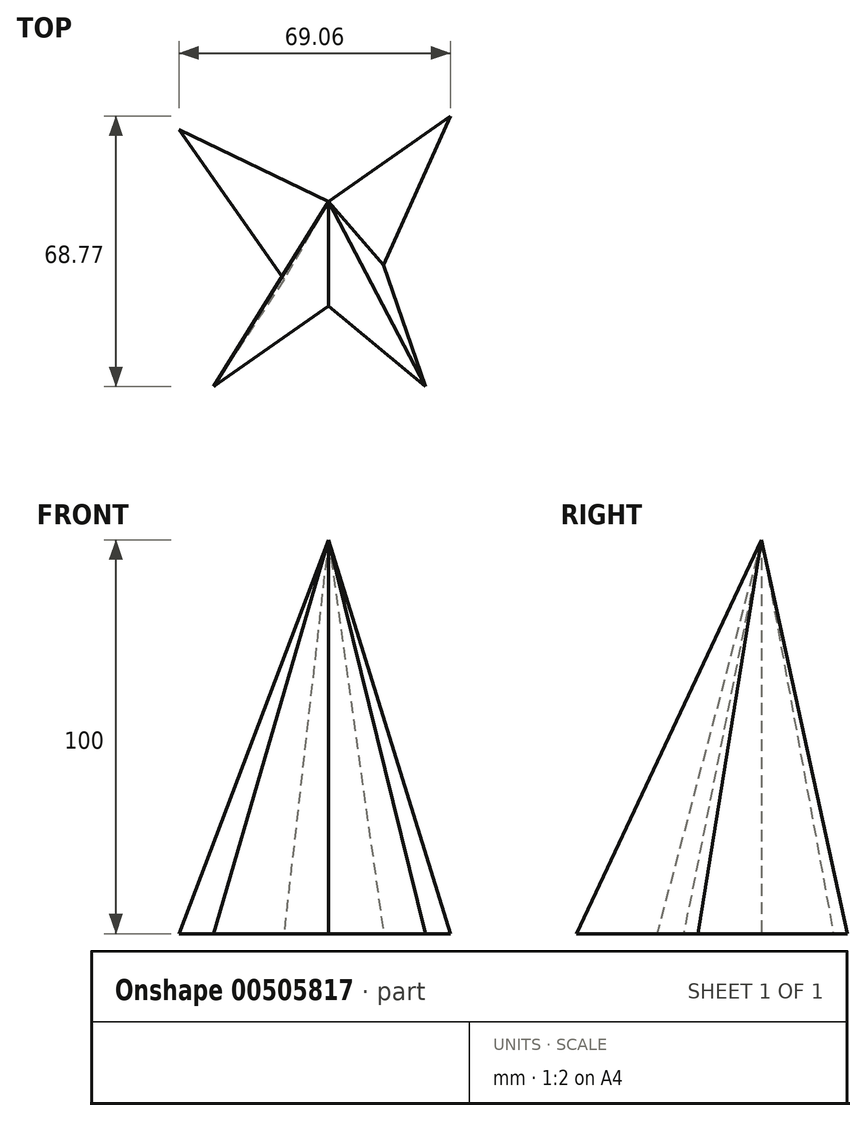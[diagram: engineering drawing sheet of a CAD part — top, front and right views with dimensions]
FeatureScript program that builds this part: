
annotation { "Feature Type Name" : "Feature", "Feature Type Description" : "" }
export const myFeature = defineFeature(function(context is Context, id is Id, definition is map)
    precondition{}
    {
        {
            var Q0;
            Q0=qCreatedBy(makeId("Top.planeOp"),FACE);
            var sketch = newSketch(context, id + "F0", { "sketchPlane" : qUnion([Q0])});
            skLineSegment(sketch, "E0", {"start": v(0, 0) * mm, "end": v(-37.97, 18.27) * mm});
            skLineSegment(sketch, "E1", {"start": v(0, 0) * mm, "end": v(31.09, 21.8) * mm});
            skLineSegment(sketch, "E2", {"start": v(31.09, 21.8) * mm, "end": v(14.04, -16.11) * mm});
            skLineSegment(sketch, "E3", {"start": v(-37.97, 18.27) * mm, "end": v(-11.28, -19.8) * mm});
            skLineSegment(sketch, "E4", {"start": v(-11.28, -19.8) * mm, "end": v(-29.16, -46.97) * mm});
            skLineSegment(sketch, "E5", {"start": v(-29.16, -46.97) * mm, "end": v(0, -26.53) * mm});
            skLineSegment(sketch, "E6", {"start": v(0, -26.53) * mm, "end": v(24.62, -46.97) * mm});
            skLineSegment(sketch, "E7", {"start": v(24.62, -46.97) * mm, "end": v(14.04, -16.11) * mm});
            skSolve(sketch);
        }
        {
            var Q0;
            Q0=qCreatedBy(makeId("Top.planeOp"),FACE);
            cPlane(context, id + "F1", {"entities" : qUnion([Q0]), "cplaneType" : CPlaneType.OFFSET, "offset" : 100 * mm, "width" : 150 * mm, "height" : 150 * mm});
        }
        {
            var Q0;
            Q0=qCreatedBy(id+"F1.planeOp",FACE);
            var sketch = newSketch(context, id + "F2", { "sketchPlane" : qUnion([Q0])});
            skPoint(sketch, "E8", {"position": v(0, 0) * mm});
            skSolve(sketch);
        }
        {
            var Q0;
            Q0=sQuery(id+"F2.wireOp",VERTEX,"E8");
            var Q1;
            Q1=makeQuery(id+"F0.imprint","IMPRINT",FACE,{"disambiguationData":[TD([[makeQuery(id+"F0.imprint","IMPRINT",EDGE,{"derivedFrom":sQuery(id+"F0.wireOp",EDGE,"E0")}),1.0]])]});
            loft(context, id + "F3", {"sheetProfilesArray" : [{ "sheetProfileEntities" : qUnion([Q0]) }, { "sheetProfileEntities" : qUnion([Q1]) }]});
        }
    });
